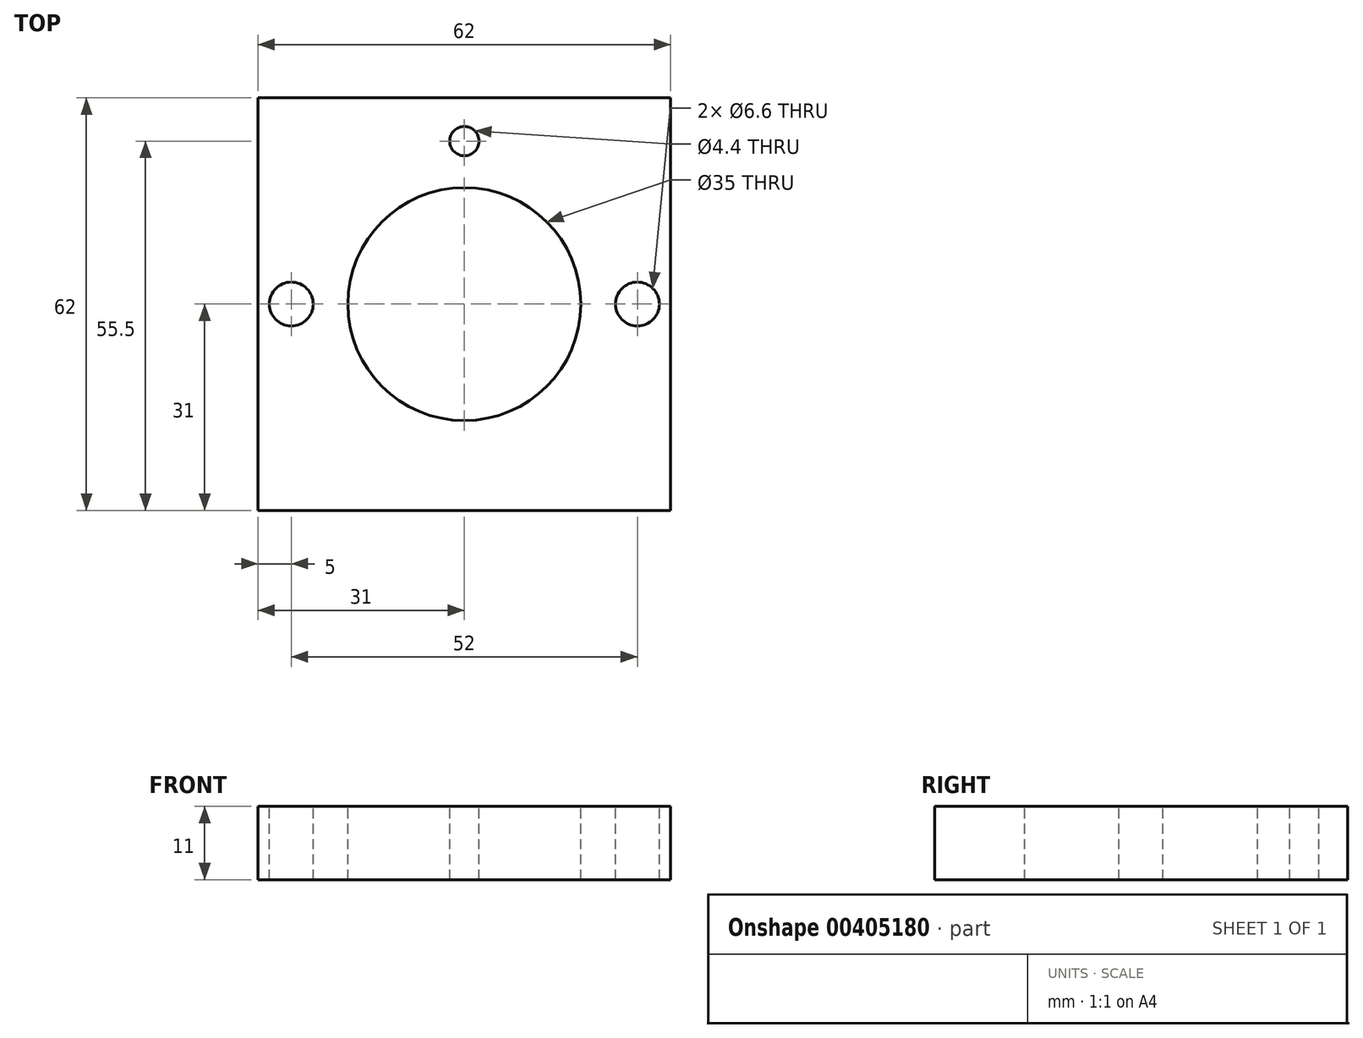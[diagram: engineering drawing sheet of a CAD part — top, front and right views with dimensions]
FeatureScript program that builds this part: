
annotation { "Feature Type Name" : "Feature", "Feature Type Description" : "" }
export const myFeature = defineFeature(function(context is Context, id is Id, definition is map)
    precondition{}
    {
        {
            var Q0;
            Q0=qCreatedBy(makeId("Top.planeOp"),FACE);
            var sketch = newSketch(context, id + "F0", { "sketchPlane" : qUnion([Q0])});
            skLineSegment(sketch, "E0.bottom", {"start": v(0, 0) * mm, "end": v(62, 0) * mm});
            skLineSegment(sketch, "E0.top", {"start": v(0, 62) * mm, "end": v(62, 62) * mm});
            skLineSegment(sketch, "E0.left", {"start": v(0, 0) * mm, "end": v(0, 62) * mm});
            skLineSegment(sketch, "E0.right", {"start": v(62, 0) * mm, "end": v(62, 62) * mm});
            skSolve(sketch);
        }
        {
            var Q0;
            Q0=makeQuery(id+"F0.imprint","IMPRINT",FACE,{"disambiguationData":[TD([[makeQuery(id+"F0.imprint","IMPRINT",EDGE,{"derivedFrom":sQuery(id+"F0.wireOp",EDGE,"E0.bottom")}),1.0]])]});
            extrude(context, id + "F1", {"entities" : qUnion([Q0]), "depth" : 11 * mm});
        }
        {
            var Q0;
            Q0=makeQuery(id+"F1.opExtrude","CAP_FACE",FACE,{"disambiguationData":[OSD([sQuery(id+"F0.wireOp",EDGE,"E0.bottom"),sQuery(id+"F0.wireOp",EDGE,"E0.top"),sQuery(id+"F0.wireOp",EDGE,"E0.left"),sQuery(id+"F0.wireOp",EDGE,"E0.right")])],"isStart":false});
            var sketch = newSketch(context, id + "F2", { "sketchPlane" : qUnion([Q0])});
            skCircle(sketch, "E1", {"center": v(5, 31) * mm, "radius": 3 * mm});
            skCircle(sketch, "E2", {"center": v(57, 31) * mm, "radius": 3 * mm});
            skSolve(sketch);
        }
        {
            var Q0;
            Q0=sQuery(id+"F2.wireOp",VERTEX,"E1.center");
            var Q1;
            Q1=sQuery(id+"F2.wireOp",VERTEX,"E2.center");
            var Q2;
            Q2=makeQuery(id+"F1.opExtrude","SWEPT_BODY",BODY,{"disambiguationData":[OSD([sQuery(id+"F0.wireOp",EDGE,"E0.bottom"),sQuery(id+"F0.wireOp",EDGE,"E0.top"),sQuery(id+"F0.wireOp",EDGE,"E0.left"),sQuery(id+"F0.wireOp",EDGE,"E0.right")])]});
            hole(context, id + "F3", {"style" : HoleStyle.SIMPLE, "endStyle" : HoleEndStyle.THROUGH, "standardTappedOrClearance" : lookupTablePath({ "standard" : "ISO", "fit" : "Normal", "size" : "M6", "type" : "Clearance" }), "standardBlindInLast" : lookupTablePath({ "fit" : "Standard", "standard" : "ISO", "size" : "M6", "type" : "Clearance" }), "holeDiameter" : 6.6 * mm, "isTappedThrough" : true, "tappedDepth" : 12 * mm, "tapClearance" : 3, "locations" : qUnion([Q0, Q1]), "scope" : qUnion([Q2])});
        }
        {
            var Q0;
            Q0=makeQuery(id+"F1.opExtrude","CAP_FACE",FACE,{"disambiguationData":[OSD([sQuery(id+"F0.wireOp",EDGE,"E0.bottom"),sQuery(id+"F0.wireOp",EDGE,"E0.top"),sQuery(id+"F0.wireOp",EDGE,"E0.left"),sQuery(id+"F0.wireOp",EDGE,"E0.right")])],"isStart":false});
            var sketch = newSketch(context, id + "F4", { "sketchPlane" : qUnion([Q0])});
            skLineSegment(sketch, "E3", {"start": v(31, 62) * mm, "end": v(31, 0) * mm});
            skCircle(sketch, "E4", {"center": v(31, 55.5) * mm, "radius": 2 * mm});
            skSolve(sketch);
        }
        {
            var Q0;
            Q0=sQuery(id+"F4.wireOp",VERTEX,"E4.center");
            var Q1;
            Q1=makeQuery(id+"F1.opExtrude","SWEPT_BODY",BODY,{"disambiguationData":[OSD([sQuery(id+"F0.wireOp",EDGE,"E0.bottom"),sQuery(id+"F0.wireOp",EDGE,"E0.top"),sQuery(id+"F0.wireOp",EDGE,"E0.left"),sQuery(id+"F0.wireOp",EDGE,"E0.right")])]});
            hole(context, id + "F5", {"style" : HoleStyle.SIMPLE, "endStyle" : HoleEndStyle.THROUGH, "standardTappedOrClearance" : lookupTablePath({ "standard" : "ISO", "fit" : "Normal", "size" : "M4", "type" : "Clearance" }), "standardBlindInLast" : lookupTablePath({ "fit" : "Standard", "standard" : "ISO", "size" : "M4", "type" : "Clearance" }), "holeDiameter" : 4.4 * mm, "isTappedThrough" : true, "tappedDepth" : 12 * mm, "tapClearance" : 3, "locations" : qUnion([Q0]), "scope" : qUnion([Q1])});
        }
        {
            var Q0;
            Q0=makeQuery(id+"F1.opExtrude","CAP_FACE",FACE,{"disambiguationData":[OSD([sQuery(id+"F0.wireOp",EDGE,"E0.bottom"),sQuery(id+"F0.wireOp",EDGE,"E0.top"),sQuery(id+"F0.wireOp",EDGE,"E0.left"),sQuery(id+"F0.wireOp",EDGE,"E0.right")])],"isStart":false});
            var sketch = newSketch(context, id + "F6", { "sketchPlane" : qUnion([Q0])});
            skCircle(sketch, "E5", {"center": v(31, 31) * mm, "radius": 17.5 * mm});
            skSolve(sketch);
        }
        {
            var Q0;
            Q0=makeQuery(id+"F6.imprint","IMPRINT",FACE,{"disambiguationData":[TD([[makeQuery(id+"F6.imprint","IMPRINT",EDGE,{"derivedFrom":sQuery(id+"F6.wireOp",EDGE,"E5")}),1.0]])]});
            extrude(context, id + "F7", {"entities" : qUnion([Q0]), "operationType" : NewBodyOperationType.REMOVE, "endBound" : BoundingType.THROUGH_ALL, "oppositeDirection" : true, "depth" : 25 * mm});
        }
    });
